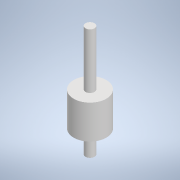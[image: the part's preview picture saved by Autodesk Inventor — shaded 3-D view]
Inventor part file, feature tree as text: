
AUTODESK INVENTOR PART (.ipt)
format: ipt  version: 2020 (Build 240168000, 168)  size: 102,400 bytes
history: native  units: mm
features: extrude x2, sketch x2
ambient origin geometry x8: Origin, YZ Plane, XZ Plane, XY Plane, X Axis, Y Axis, Z Axis, Center Point
bodies: Solido1 (feature_tree)
feature tree (4):
  extrude  "Estrusione1"  Depth=29.0mm
  extrude  "Estrusione2"  Depth=30.0mm TaperAngle=0.0deg
  sketch  "Schizzo1"
  sketch  "Schizzo2"
